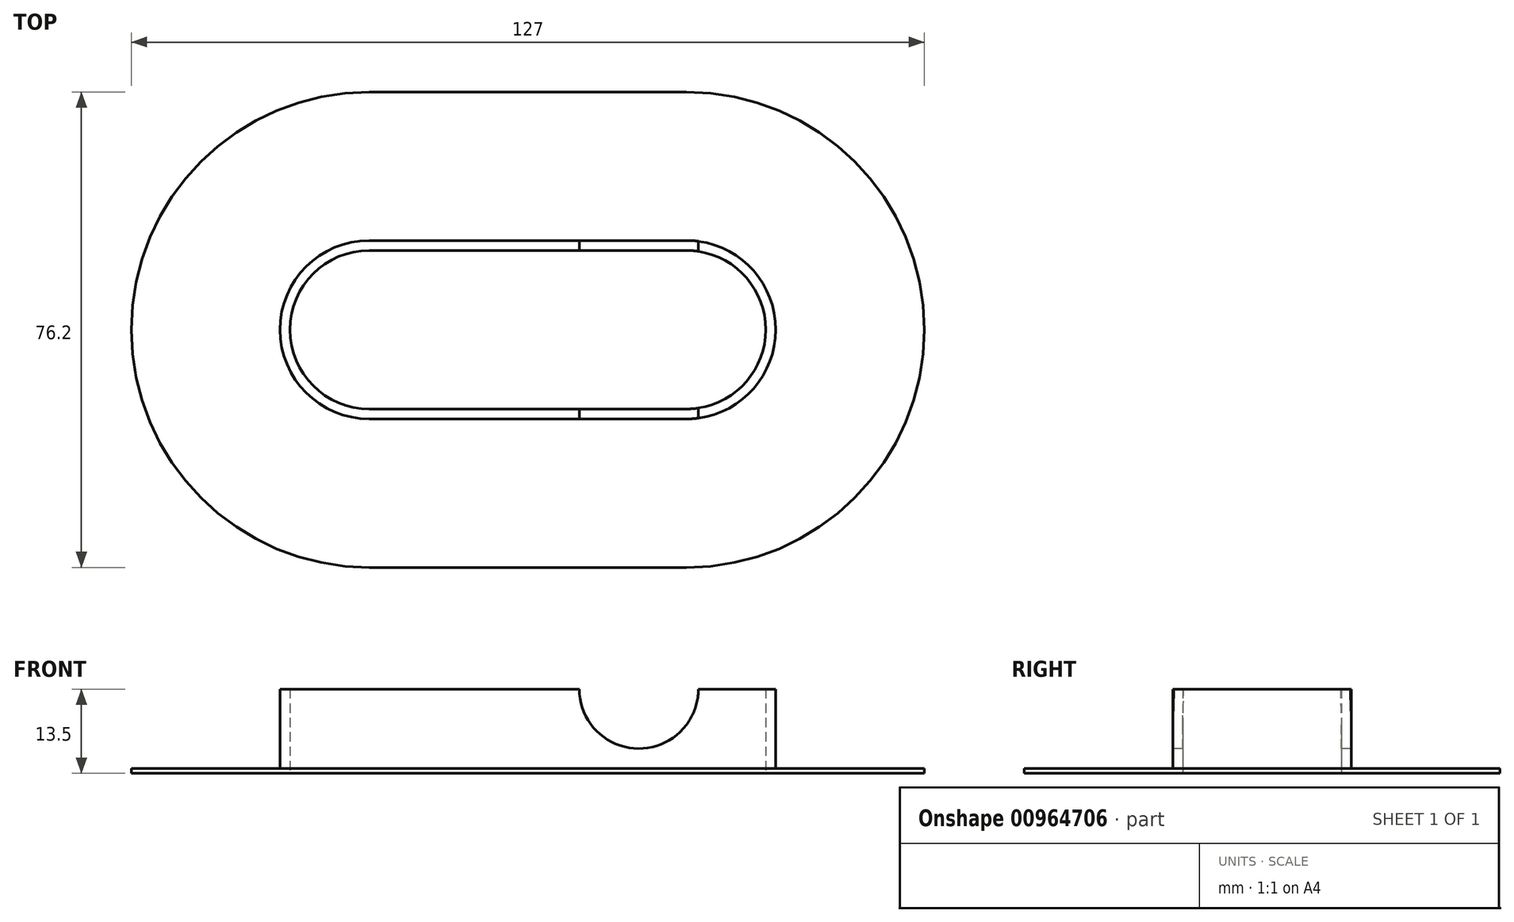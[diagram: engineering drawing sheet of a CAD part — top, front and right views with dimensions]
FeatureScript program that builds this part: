
annotation { "Feature Type Name" : "Feature", "Feature Type Description" : "" }
export const myFeature = defineFeature(function(context is Context, id is Id, definition is map)
    precondition{}
    {
        {
            var Q0;
            Q0=qCreatedBy(makeId("Top.planeOp"),FACE);
            var sketch = newSketch(context, id + "F0", { "sketchPlane" : qUnion([Q0])});
            skLineSegment(sketch, "E0.right", {"start": v(27.35, 4.89) * mm, "end": v(27.35, -20.51) * mm});
            skLineSegment(sketch, "E1.bottom", {"start": v(27.35, -20.51) * mm, "end": v(1.95, -20.51) * mm});
            skLineSegment(sketch, "E1.left", {"start": v(27.35, -20.51) * mm, "end": v(27.35, -20.51) * mm});
            skPoint(sketch, "E2", {"position": v(27.35, -7.81) * mm});
            skCircle(sketch, "E3", {"center": v(27.35, -7.81) * mm, "radius": 0.48 * mm});
            skPoint(sketch, "E4", {"position": v(39.54, -11.37) * mm});
            skArc(sketch, "E5", {"start": v(27.35, -20.51) * mm, "mid": v(40.05, -7.81) * mm, "end": v(27.35, 4.89) * mm});
            skArc(sketch, "E6.1", {"start": v(27.35, -45.91) * mm, "mid": v(65.45, -7.81) * mm, "end": v(27.35, 30.29) * mm});
            skLineSegment(sketch, "E7.0", {"start": v(27.35, -45.91) * mm, "end": v(1.95, -45.91) * mm});
            skLineSegment(sketch, "E8", {"start": v(27.35, 4.89) * mm, "end": v(27.35, 30.29) * mm});
            skLineSegment(sketch, "E9", {"start": v(27.35, -20.51) * mm, "end": v(27.35, -45.91) * mm});
            skLineSegment(sketch, "E10", {"start": v(65.45, -7.81) * mm, "end": v(1.95, -7.81) * mm});
            skPoint(sketch, "E11.startSnap0", {"position": v(2.13, -45.91) * mm});
            skLineSegment(sketch, "E12", {"start": v(1.95, 30.29) * mm, "end": v(27.35, 30.29) * mm});
            skLineSegment(sketch, "E13", {"start": v(1.95, 4.89) * mm, "end": v(27.35, 4.89) * mm});
            skCircle(sketch, "E14.MirrorC", {"center": v(-23.45, -7.81) * mm, "radius": 0.48 * mm});
            skPoint(sketch, "E15.MirrorP", {"position": v(-35.64, -11.37) * mm});
            skLineSegment(sketch, "E16.MirrorCS", {"start": v(-23.45, 4.89) * mm, "end": v(-23.45, 30.29) * mm});
            skPoint(sketch, "E17.MirrorP", {"position": v(1.77, -45.91) * mm});
            skLineSegment(sketch, "E18.MirrorCS", {"start": v(1.95, 4.89) * mm, "end": v(-23.45, 4.89) * mm});
            skLineSegment(sketch, "E19.MirrorCS", {"start": v(-23.45, -45.91) * mm, "end": v(1.95, -45.91) * mm});
            skArc(sketch, "E20.MirrorCS", {"start": v(-23.45, -20.51) * mm, "mid": v(-36.15, -7.81) * mm, "end": v(-23.45, 4.89) * mm});
            skLineSegment(sketch, "E21.MirrorCS", {"start": v(-23.45, -20.51) * mm, "end": v(1.95, -20.51) * mm});
            skArc(sketch, "E22.MirrorCS", {"start": v(-23.45, -45.91) * mm, "mid": v(-61.55, -7.81) * mm, "end": v(-23.45, 30.29) * mm});
            skLineSegment(sketch, "E23.MirrorCS", {"start": v(-23.45, -20.51) * mm, "end": v(-23.45, -45.91) * mm});
            skLineSegment(sketch, "E24.MirrorCS", {"start": v(-61.55, -7.81) * mm, "end": v(1.95, -7.81) * mm});
            skLineSegment(sketch, "E25.MirrorCS", {"start": v(-23.45, 4.89) * mm, "end": v(-23.45, -20.51) * mm});
            skLineSegment(sketch, "E26.MirrorCS", {"start": v(1.95, 30.29) * mm, "end": v(-23.45, 30.29) * mm});
            skSolve(sketch);
        }
        {
            var Q0;
            Q0=makeQuery(id+"F0.imprint","IMPRINT",FACE,{"disambiguationData":[TD([[makeQuery(id+"F0.imprint","IMPRINT",EDGE,{"derivedFrom":sQuery(id+"F0.wireOp",EDGE,"E8")}),1.0]])]});
            var Q1;
            {var subQ0=sQuery(id+"F0.wireOp",EDGE,"E8");Q1=makeQuery(id+"F0.imprint","IMPRINT",FACE,{"disambiguationData":[TD([[makeQuery(id+"F0.imprint","IMPRINT",EDGE,{"derivedFrom":subQ0}),-1.0]])]});}
            var Q2;
            {var subQ0=sQuery(id+"F0.wireOp",EDGE,"E9");Q2=makeQuery(id+"F0.imprint","IMPRINT",FACE,{"disambiguationData":[TD([[makeQuery(id+"F0.imprint","IMPRINT",EDGE,{"derivedFrom":subQ0}),1.0]])]});}
            var Q3;
            Q3=makeQuery(id+"F0.imprint","IMPRINT",FACE,{"disambiguationData":[TD([[makeQuery(id+"F0.imprint","IMPRINT",EDGE,{"derivedFrom":sQuery(id+"F0.wireOp",EDGE,"E1.bottom")}),1.0]])]});
            var Q4;
            {var subQ0=sQuery(id+"F0.wireOp",EDGE,"E23.MirrorCS");Q4=makeQuery(id+"F0.imprint","IMPRINT",FACE,{"disambiguationData":[TD([[makeQuery(id+"F0.imprint","IMPRINT",EDGE,{"derivedFrom":subQ0}),-1.0]])]});}
            var Q5;
            {var subQ0=sQuery(id+"F0.wireOp",EDGE,"E16.MirrorCS");Q5=makeQuery(id+"F0.imprint","IMPRINT",FACE,{"disambiguationData":[TD([[makeQuery(id+"F0.imprint","IMPRINT",EDGE,{"derivedFrom":subQ0}),1.0]])]});}
            extrude(context, id + "F1", {"entities" : qUnion([Q0, Q1, Q2, Q3, Q4, Q5]), "depth" : 0.8 * mm, "offsetDistance" : 25.4 * mm});
        }
        {
            var Q0;
            Q0=makeQuery(id+"F1.opExtrude","CAP_FACE",FACE,{"disambiguationData":[OSD([sQuery(id+"F0.wireOp",EDGE,"E1.bottom"),sQuery(id+"F0.wireOp",EDGE,"E5"),sQuery(id+"F0.wireOp",EDGE,"E6.1"),sQuery(id+"F0.wireOp",EDGE,"E7.0"),sQuery(id+"F0.wireOp",EDGE,"E12"),sQuery(id+"F0.wireOp",EDGE,"E13"),sQuery(id+"F0.wireOp",EDGE,"E18.MirrorCS"),sQuery(id+"F0.wireOp",EDGE,"E19.MirrorCS"),sQuery(id+"F0.wireOp",EDGE,"E20.MirrorCS"),sQuery(id+"F0.wireOp",EDGE,"E21.MirrorCS"),sQuery(id+"F0.wireOp",EDGE,"E22.MirrorCS"),sQuery(id+"F0.wireOp",EDGE,"E26.MirrorCS")])],"isStart":false});
            var sketch = newSketch(context, id + "F2", { "sketchPlane" : qUnion([Q0])});
            skLineSegment(sketch, "E27.0", {"start": v(27.35, 4.89) * mm, "end": v(-23.45, 4.89) * mm});
            skArc(sketch, "E27.1", {"start": v(27.35, -20.51) * mm, "mid": v(40.05, -7.81) * mm, "end": v(27.35, 4.89) * mm});
            skLineSegment(sketch, "E27.2", {"start": v(27.35, -20.51) * mm, "end": v(-23.45, -20.51) * mm});
            skArc(sketch, "E27.3", {"start": v(-23.45, -20.51) * mm, "mid": v(-36.15, -7.81) * mm, "end": v(-23.45, 4.89) * mm});
            skLineSegment(sketch, "E28.0", {"start": v(27.35, 6.49) * mm, "end": v(-23.45, 6.49) * mm});
            skArc(sketch, "E28.1", {"start": v(27.35, -22.11) * mm, "mid": v(41.65, -7.81) * mm, "end": v(27.35, 6.49) * mm});
            skLineSegment(sketch, "E28.2", {"start": v(27.35, -22.11) * mm, "end": v(-23.45, -22.11) * mm});
            skArc(sketch, "E28.3", {"start": v(-23.45, -22.11) * mm, "mid": v(-37.75, -7.81) * mm, "end": v(-23.45, 6.49) * mm});
            skSolve(sketch);
        }
        {
            var Q0;
            Q0=makeQuery(id+"F2.imprint","IMPRINT",FACE,{"disambiguationData":[TD([[makeQuery(id+"F2.imprint","IMPRINT",EDGE,{"derivedFrom":sQuery(id+"F2.wireOp",EDGE,"E27.0")}),-1.0]])]});
            extrude(context, id + "F3", {"entities" : qUnion([Q0]), "operationType" : NewBodyOperationType.ADD, "depth" : 12.7 * mm, "offsetDistance" : 25.4 * mm});
        }
        {
            var Q0;
            Q0=makeQuery(id+"F3.opExtrude","SWEPT_FACE",FACE,{"disambiguationData":[OSD([sQuery(id+"F2.wireOp",EDGE,"E28.2")])]});
            var sketch = newSketch(context, id + "F4", { "sketchPlane" : qUnion([Q0])});
            skLineSegment(sketch, "E29.bottom", {"start": v(27.35, 13.5) * mm, "end": v(19.73, 13.5) * mm});
            skLineSegment(sketch, "E29.top", {"start": v(27.35, 0.8) * mm, "end": v(19.73, 0.8) * mm});
            skLineSegment(sketch, "E29.left", {"start": v(27.35, 13.5) * mm, "end": v(27.35, 0.8) * mm});
            skLineSegment(sketch, "E29.right", {"start": v(19.73, 13.5) * mm, "end": v(19.73, 0.8) * mm});
            skSolve(sketch);
        }
        {
            var Q0;
            Q0=sQuery(id+"F4.wireOp",VERTEX,"E29.bottom.end");
            var Q1;
            Q1=makeQuery(id+"F1.opExtrude","SWEPT_BODY",BODY,{"disambiguationData":[OSD([sQuery(id+"F0.wireOp",EDGE,"E1.bottom"),sQuery(id+"F0.wireOp",EDGE,"E5"),sQuery(id+"F0.wireOp",EDGE,"E6.1"),sQuery(id+"F0.wireOp",EDGE,"E7.0"),sQuery(id+"F0.wireOp",EDGE,"E12"),sQuery(id+"F0.wireOp",EDGE,"E13"),sQuery(id+"F0.wireOp",EDGE,"E18.MirrorCS"),sQuery(id+"F0.wireOp",EDGE,"E19.MirrorCS"),sQuery(id+"F0.wireOp",EDGE,"E20.MirrorCS"),sQuery(id+"F0.wireOp",EDGE,"E21.MirrorCS"),sQuery(id+"F0.wireOp",EDGE,"E22.MirrorCS"),sQuery(id+"F0.wireOp",EDGE,"E26.MirrorCS")])]});
            hole(context, id + "F5", {"style" : HoleStyle.SIMPLE, "endStyle" : HoleEndStyle.THROUGH, "holeDiameter" : 19.05 * mm, "majorDiameter" : 6.35 * mm, "isTappedThrough" : true, "tappedDepth" : 12.7 * mm, "tapClearance" : 3, "locations" : qUnion([Q0]), "scope" : qUnion([Q1])});
        }
    });
